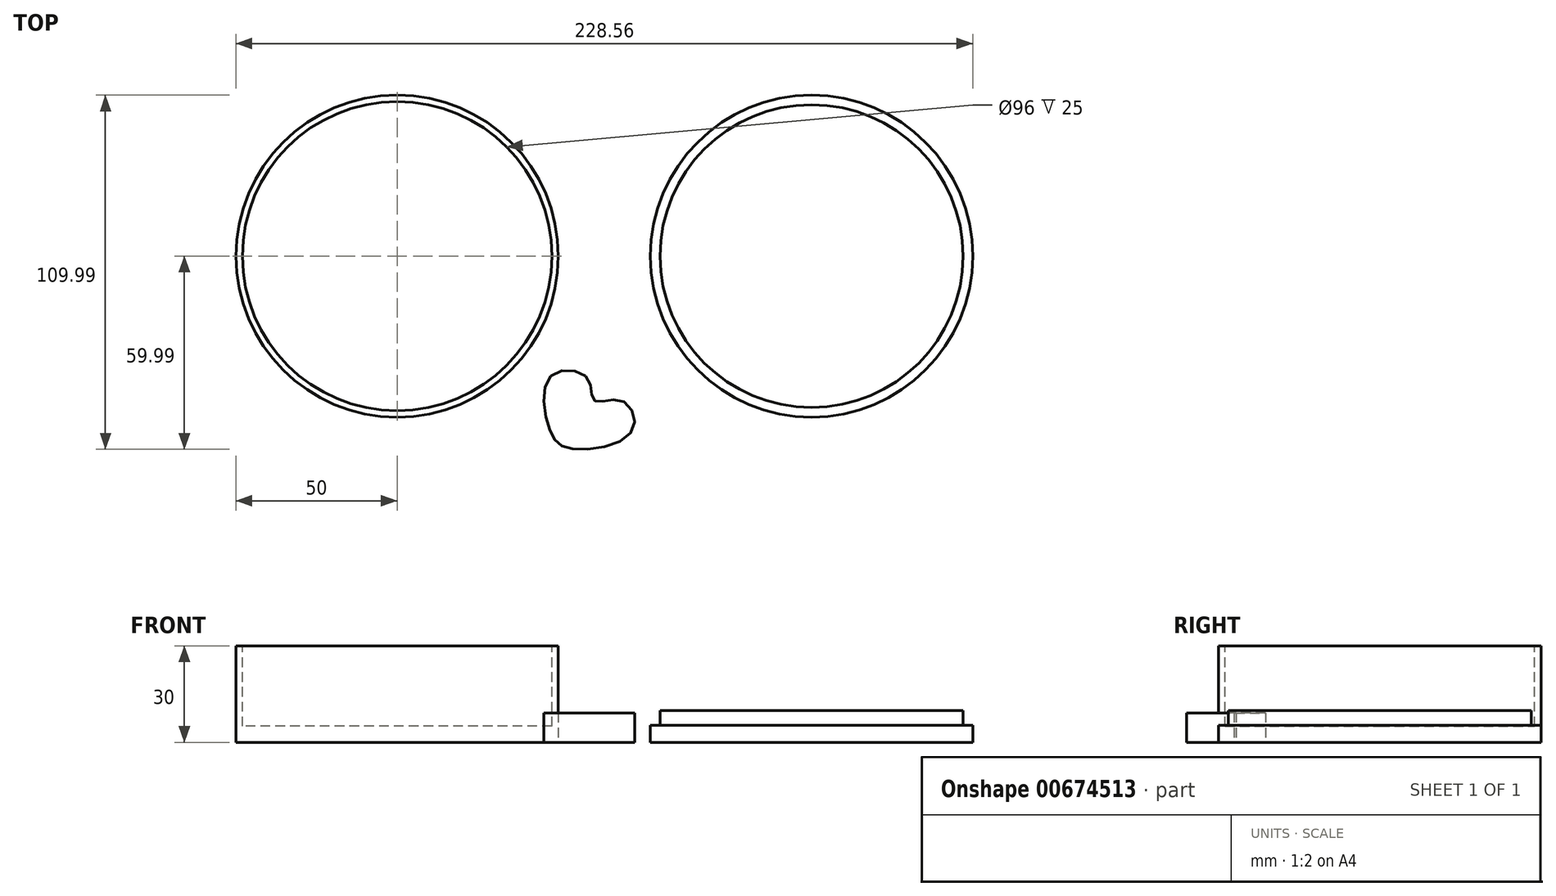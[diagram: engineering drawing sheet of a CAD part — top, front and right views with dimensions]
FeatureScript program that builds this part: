
annotation { "Feature Type Name" : "Feature", "Feature Type Description" : "" }
export const myFeature = defineFeature(function(context is Context, id is Id, definition is map)
    precondition{}
    {
        {
            var Q0;
            Q0=qCreatedBy(makeId("Top.planeOp"),FACE);
            var sketch = newSketch(context, id + "F0", { "sketchPlane" : qUnion([Q0])});
            skCircle(sketch, "E0", {"center": v(0, 0) * mm, "radius": 50 * mm});
            skSolve(sketch);
        }
        {
            var Q0;
            Q0=makeQuery(id+"F0.imprint","IMPRINT",FACE,{"disambiguationData":[TD([[makeQuery(id+"F0.imprint","IMPRINT",EDGE,{"derivedFrom":sQuery(id+"F0.wireOp",EDGE,"E0")}),1.0]])]});
            extrude(context, id + "F1", {"entities" : qUnion([Q0]), "depth" : 30 * mm, "offsetDistance" : 25.4 * mm});
        }
        {
            var Q0;
            Q0=makeQuery(id+"F1.opExtrude","CAP_FACE",FACE,{"disambiguationData":[OSD([sQuery(id+"F0.wireOp",EDGE,"E0")])],"isStart":false});
            var sketch = newSketch(context, id + "F2", { "sketchPlane" : qUnion([Q0])});
            skCircle(sketch, "E1", {"center": v(0, 0) * mm, "radius": 48 * mm});
            skSolve(sketch);
        }
        {
            var Q0;
            Q0 = qSketchRegion(id + "F2", true);
            extrude(context, id + "F3", {"entities" : qUnion([Q0]), "operationType" : NewBodyOperationType.REMOVE, "oppositeDirection" : true, "depth" : 25 * mm, "offsetDistance" : 25.4 * mm});
        }
        {
            var Q0;
            Q0=qCreatedBy(makeId("Top.planeOp"),FACE);
            var sketch = newSketch(context, id + "F4", { "sketchPlane" : qUnion([Q0])});
            skCircle(sketch, "E2", {"center": v(128.56, 0) * mm, "radius": 50 * mm});
            skSolve(sketch);
        }
        {
            var Q0;
            Q0=makeQuery(id+"F4.imprint","IMPRINT",FACE,{"disambiguationData":[TD([[makeQuery(id+"F4.imprint","IMPRINT",EDGE,{"derivedFrom":sQuery(id+"F4.wireOp",EDGE,"E2")}),1.0]])]});
            extrude(context, id + "F5", {"entities" : qUnion([Q0]), "depth" : 5.33 * mm, "offsetDistance" : 25.4 * mm});
        }
        {
            var Q0;
            Q0=makeQuery(id+"F5.opExtrude","CAP_FACE",FACE,{"disambiguationData":[OSD([sQuery(id+"F4.wireOp",EDGE,"E2")])],"isStart":false});
            var sketch = newSketch(context, id + "F6", { "sketchPlane" : qUnion([Q0])});
            skCircle(sketch, "E3", {"center": v(128.56, 0) * mm, "radius": 47 * mm});
            skSolve(sketch);
        }
        {
            var Q0;
            Q0 = qSketchRegion(id + "F6", true);
            extrude(context, id + "F7", {"entities" : qUnion([Q0]), "operationType" : NewBodyOperationType.ADD, "depth" : 4.57 * mm, "offsetDistance" : 25.4 * mm});
        }
        {
            var Q0;
            Q0=qCreatedBy(makeId("Top.planeOp"),FACE);
            var sketch = newSketch(context, id + "F8", { "sketchPlane" : qUnion([Q0])});
            skFitSpline(sketch, "E4", {"points": [v(47.4, -54.08) * mm, v(47.67, -37.3) * mm, v(59.04, -37.84) * mm, v(61.2, -44.88) * mm, v(69.6, -44.88) * mm, v(72.84, -54.35) * mm, v(53.9, -59.77) * mm, v(47.4, -54.08) * mm]});
            skSolve(sketch);
        }
        {
            var Q0;
            Q0=makeQuery(id+"F8.imprint","IMPRINT",FACE,{"disambiguationData":[TD([[makeQuery(id+"F8.imprint","IMPRINT",EDGE,{"derivedFrom":sQuery(id+"F8.wireOp",EDGE,"E4")}),-1.0]])]});
            var sketch = newSketch(context, id + "F9", { "sketchPlane" : qUnion([Q0])});
            skSolve(sketch);
        }
        {
            var Q0;
            Q0 = qSketchRegion(id + "F9", true);
            var Q1;
            Q1=makeQuery(id+"F8.imprint","IMPRINT",FACE,{"disambiguationData":[TD([[makeQuery(id+"F8.imprint","IMPRINT",EDGE,{"derivedFrom":sQuery(id+"F8.wireOp",EDGE,"E4")}),-1.0]])]});
            extrude(context, id + "F10", {"entities" : qUnion([Q0, Q1]), "depth" : 9.14 * mm, "offsetDistance" : 25.4 * mm});
        }
    });
